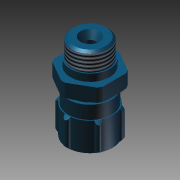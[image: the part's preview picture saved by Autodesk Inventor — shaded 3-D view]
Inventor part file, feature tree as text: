
AUTODESK INVENTOR PART (.ipt)
format: ipt  version: 2016 (Build 200138000, 138)  size: 268,800 bytes
history: native  units: mm
features: other x7, sketch x7, revolve x5, thread x2, extrude x2
ambient origin geometry x8: Origin, YZ Plane, XZ Plane, XY Plane, X Axis, Y Axis, Z Axis, Center Point
bodies: Solid1 (feature_tree)
feature tree (23):
  revolve  "Revolution1"  Angle=360.0deg
  revolve  "Revolution2"  [1 undecoded]
  thread  "Thread1"  [1 undecoded]
  extrude  "Extrusion1"  Depth=4.319mm TaperAngle=0.0deg
  revolve  "Revolution3"  Angle=360.0deg
  revolve  "Revolution4"  [1 undecoded]
  thread  "Thread2"  [1 undecoded]
  extrude  "Extrusion2"  [1 undecoded]
  revolve  "Revolution5"  [1 undecoded]
  other  "ANBAU_XY"
  other  "ANBAU_YZ"
  other  "ANBAU_ZX"
  other  "ANBAU_X"
  other  "ANBAU_Y"
  other  "ANBAU_Z"
  other  "ANBAU_Center"
  sketch  "Sketch_1"  dims[d0=360.0deg d1=360.0deg]
  sketch  "Sketch_2"  dims[d7=360.0deg d8=4.319mm d9=0.0mm]
  sketch  "Sketch_3"  dims[d10=3.7mm d11=0.0mm d12=360.0deg]
  sketch  "Sketch_4"  dims[d13=0.0mm]
  sketch  "Sketch_5"
  sketch  "Sketch_6"
  sketch  "Sketch_7_ALT_Drilling_1"  dims[d2=5.9585mm d3=0.0mm d4=7.5mm d5=0.0mm d6=360.0deg]
note: 6 required parameter values undecoded (feature->parameter linkage not recoverable at this tier; creation-order binding heuristic only, values carry confidence <= 0.55)